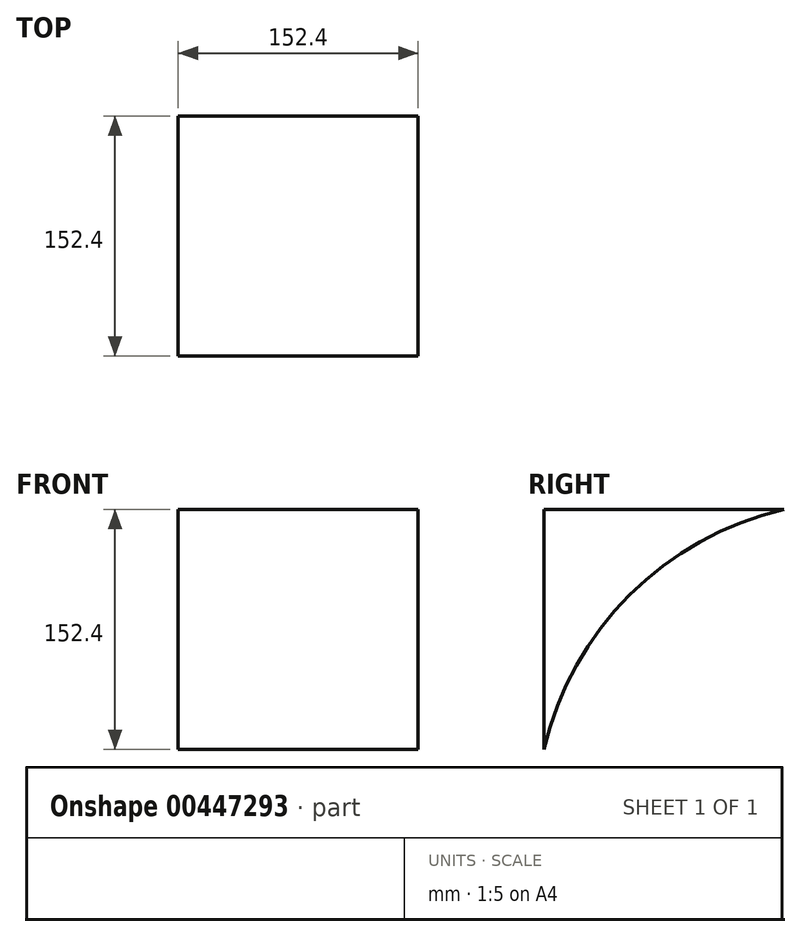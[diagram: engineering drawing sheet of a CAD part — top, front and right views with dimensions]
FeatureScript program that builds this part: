
annotation { "Feature Type Name" : "Feature", "Feature Type Description" : "" }
export const myFeature = defineFeature(function(context is Context, id is Id, definition is map)
    precondition{}
    {
        {
            var Q0;
            Q0=qCreatedBy(makeId("Right.planeOp"),FACE);
            var sketch = newSketch(context, id + "F0", { "sketchPlane" : qUnion([Q0])});
            skLineSegment(sketch, "E0", {"start": v(76.28, 77.16) * mm, "end": v(-76.12, 77.16) * mm});
            skLineSegment(sketch, "E1", {"start": v(-76.12, 77.16) * mm, "end": v(-76.12, -75.24) * mm});
            skArc(sketch, "E2", {"start": v(76.28, 77.16) * mm, "mid": v(-21.79, 22.83) * mm, "end": v(-76.12, -75.24) * mm});
            skSolve(sketch);
        }
        {
            var Q0;
            Q0=makeQuery(id+"F0.imprint","IMPRINT",FACE,{"disambiguationData":[TD([[makeQuery(id+"F0.imprint","IMPRINT",EDGE,{"derivedFrom":sQuery(id+"F0.wireOp",EDGE,"E0")}),1.0]])]});
            extrude(context, id + "F1", {"entities" : qUnion([Q0]), "depth" : 152.4 * mm});
        }
    });
